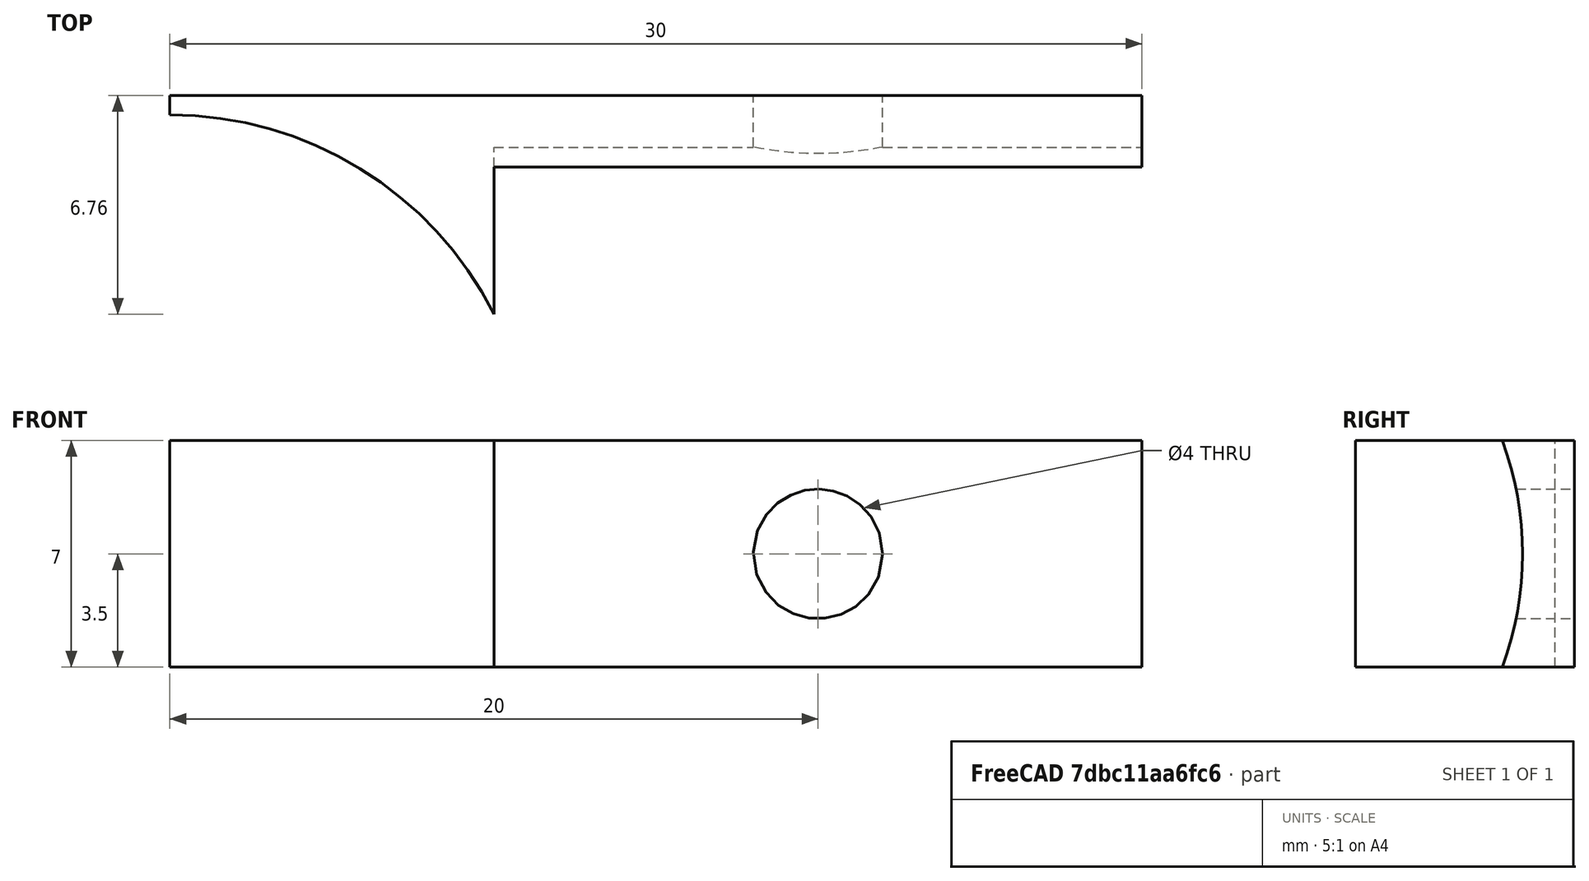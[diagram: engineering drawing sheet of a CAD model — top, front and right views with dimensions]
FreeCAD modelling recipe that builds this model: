
FCSTD DOCUMENT  (FreeCAD 0.17R13522 (Git))
Label: connector-bearing-inset
License: All rights reserved
LicenseURL: http://en.wikipedia.org/wiki/All_rights_reserved
objects: Part::Cylinder×3, Part::Box×1, Part::MultiFuse×1, Part::Cut×1
note: 6 computed .brp shape members not serialized (recipe doc carries the construction recipe); baked Part::Feature solids carry a one-line shape summary decoded from their .brp

FEATURE [Part::Box] Box  label="Cube"
  AttacherType = Attacher::AttachEngine3D
  Height = 7
  Length = 30
  Placement = pos=(0,0,-3.5) rot=(0,0,1;0rad)
  Width = 11.8
FEATURE [Part::Cylinder] Cylinder
  Angle = 360
  AttacherType = Attacher::AttachEngine3D
  Height = 20
  Placement = pos=(10,0,0) rot=(0,1,0;1.5708rad)
  Radius = 10.2
FEATURE [Part::Cylinder] Cylinder001
  Angle = 360
  AttacherType = Attacher::AttachEngine3D
  Height = 7
  Placement = pos=(0,0,-3.5) rot=(0,0,1;0rad)
  Radius = 11.2
FEATURE [Part::Cylinder] Cylinder002
  Angle = 360
  AttacherType = Attacher::AttachEngine3D
  Height = 10
  Placement = pos=(20,5,0) rot=(1,0,0;4.71239rad)
  Radius = 2
FEATURE [Part::MultiFuse] Fusion
  Shapes = -> [Cylinder,Cylinder001,Cylinder002]
FEATURE [Part::Cut] Cut
  Base = -> Box
  Tool = -> Fusion
